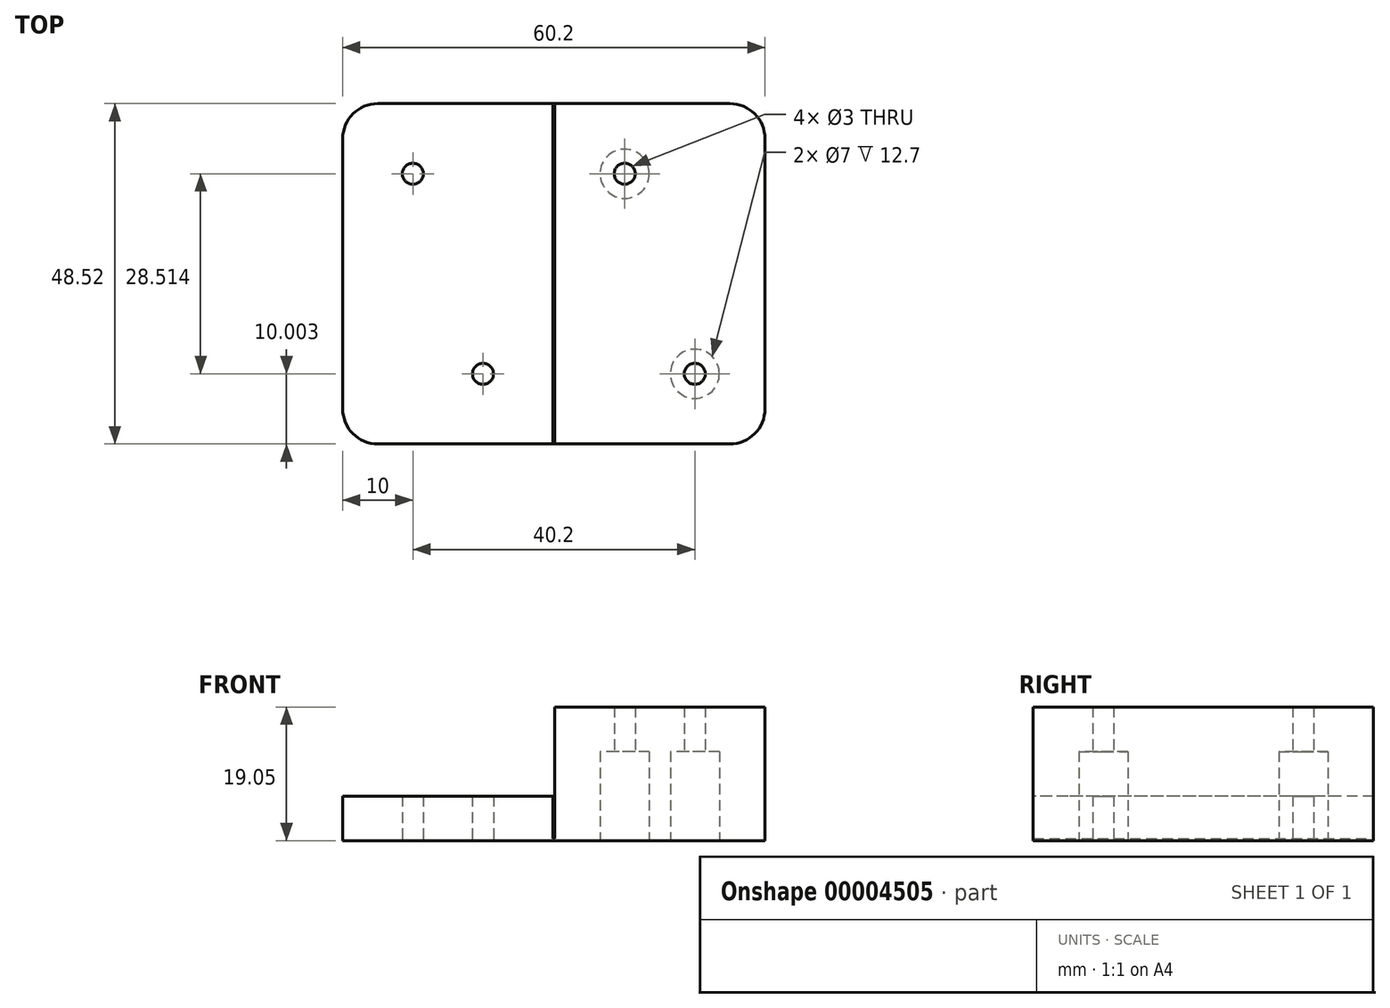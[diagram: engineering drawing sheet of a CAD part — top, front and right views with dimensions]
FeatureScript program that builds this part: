
annotation { "Feature Type Name" : "Feature", "Feature Type Description" : "" }
export const myFeature = defineFeature(function(context is Context, id is Id, definition is map)
    precondition{}
    {
        {
            var Q0;
            Q0=qCreatedBy(makeId("Top.planeOp"),FACE);
            var sketch = newSketch(context, id + "F0", { "sketchPlane" : qUnion([Q0])});
            skLineSegment(sketch, "E0.rect.bottom", {"start": v(30.1, 24.26) * mm, "end": v(-30.1, 24.26) * mm});
            skLineSegment(sketch, "E0.rect.top", {"start": v(30.1, -24.26) * mm, "end": v(-30.1, -24.26) * mm});
            skLineSegment(sketch, "E0.rect.left", {"start": v(30.1, 24.26) * mm, "end": v(30.1, -24.26) * mm});
            skLineSegment(sketch, "E0.rect.right", {"start": v(-30.1, 24.26) * mm, "end": v(-30.1, -24.26) * mm});
            skPoint(sketch, "E0.rect.middle", {"position": v(0, 0) * mm});
            skSolve(sketch);
        }
        {
            var Q0;
            Q0 = qSketchRegion(id + "F0", true);
            extrude(context, id + "F1", {"entities" : qUnion([Q0]), "depth" : .3 * mm});
        }
        {
            var Q0;
            Q0=qCreatedBy(makeId("Top.planeOp"),FACE);
            var sketch = newSketch(context, id + "F2", { "sketchPlane" : qUnion([Q0])});
            skLineSegment(sketch, "E1.bottom", {"start": v(30.1, 24.26) * mm, "end": v(0.1, 24.26) * mm});
            skLineSegment(sketch, "E1.top", {"start": v(30.1, -24.26) * mm, "end": v(0.1, -24.26) * mm});
            skLineSegment(sketch, "E1.left", {"start": v(30.1, 24.26) * mm, "end": v(30.1, -24.26) * mm});
            skLineSegment(sketch, "E1.right", {"start": v(0.1, 24.26) * mm, "end": v(0.1, -24.26) * mm});
            skSolve(sketch);
        }
        {
            var Q0;
            Q0 = qSketchRegion(id + "F2", true);
            extrude(context, id + "F3", {"entities" : qUnion([Q0]), "operationType" : NewBodyOperationType.ADD, "depth" : 19.05 * mm});
        }
        {
            var Q0;
            Q0=qCreatedBy(makeId("Top.planeOp"),FACE);
            var sketch = newSketch(context, id + "F4", { "sketchPlane" : qUnion([Q0])});
            skLineSegment(sketch, "E2.bottom", {"start": v(-30.1, 24.26) * mm, "end": v(-0.1, 24.26) * mm});
            skLineSegment(sketch, "E2.top", {"start": v(-30.1, -24.26) * mm, "end": v(-0.1, -24.26) * mm});
            skLineSegment(sketch, "E2.left", {"start": v(-30.1, 24.26) * mm, "end": v(-30.1, -24.26) * mm});
            skLineSegment(sketch, "E2.right", {"start": v(-0.1, 24.26) * mm, "end": v(-0.1, -24.26) * mm});
            skSolve(sketch);
        }
        {
            var Q0;
            Q0 = qSketchRegion(id + "F4", true);
            extrude(context, id + "F5", {"entities" : qUnion([Q0]), "operationType" : NewBodyOperationType.ADD, "depth" : 6.35 * mm});
        }
        {
            var Q0;
            Q0=qCreatedBy(makeId("Top.planeOp"),FACE);
            var sketch = newSketch(context, id + "F6", { "sketchPlane" : qUnion([Q0])});
            skCircle(sketch, "E3", {"center": v(10.1, 14.26) * mm, "radius": 1.5 * mm});
            skCircle(sketch, "E4", {"center": v(20.1, -14.26) * mm, "radius": 1.5 * mm});
            skCircle(sketch, "E5.1.0.0", {"center": v(-10.1, -14.26) * mm, "radius": 1.5 * mm});
            skCircle(sketch, "E5.1.0.1", {"center": v(-20.1, 14.26) * mm, "radius": 1.5 * mm});
            skLineSegment(sketch, "E5.direction1", {"start": v(20.1, -14.26) * mm, "end": v(-10.1, -14.26) * mm, "construction": true});
            skSolve(sketch);
        }
        {
            var Q0;
            Q0 = qSketchRegion(id + "F6", true);
            extrude(context, id + "F7", {"entities" : qUnion([Q0]), "operationType" : NewBodyOperationType.REMOVE, "endBound" : BoundingType.THROUGH_ALL, "depth" : 25 * mm});
        }
        {
            var Q0;
            Q0=qCreatedBy(makeId("Top.planeOp"),FACE);
            var sketch = newSketch(context, id + "F8", { "sketchPlane" : qUnion([Q0])});
            skCircle(sketch, "E6", {"center": v(10.1, 14.26) * mm, "radius": 3.5 * mm});
            skCircle(sketch, "E7", {"center": v(20.1, -14.26) * mm, "radius": 3.5 * mm});
            skSolve(sketch);
        }
        {
            var Q0;
            Q0 = qSketchRegion(id + "F8", true);
            extrude(context, id + "F9", {"entities" : qUnion([Q0]), "operationType" : NewBodyOperationType.REMOVE, "depth" : 12.7 * mm});
        }
        {
            var Q0;
            Q0=makeQuery(id+"F3.boolean.opBoolean","MERGE",EDGE,{"derivedFrom":[makeQuery(id+"F1.opExtrude","SWEPT_EDGE",EDGE,{"disambiguationData":[OSD([sQuery(id+"F0.wireOp",EDGE,"E0.rect.bottom"),sQuery(id+"F0.wireOp",EDGE,"E0.rect.left")])]}),makeQuery(id+"F3.opExtrude","SWEPT_EDGE",EDGE,{"disambiguationData":[OSD([sQuery(id+"F2.wireOp",EDGE,"E1.bottom"),sQuery(id+"F2.wireOp",EDGE,"E1.left")])]})]});
            var Q1;
            Q1=makeQuery(id+"F5.boolean.opBoolean","MERGE",EDGE,{"derivedFrom":[makeQuery(id+"F1.opExtrude","SWEPT_EDGE",EDGE,{"disambiguationData":[OSD([sQuery(id+"F0.wireOp",EDGE,"E0.rect.bottom"),sQuery(id+"F0.wireOp",EDGE,"E0.rect.right")])]}),makeQuery(id+"F5.opExtrude","SWEPT_EDGE",EDGE,{"disambiguationData":[OSD([sQuery(id+"F4.wireOp",EDGE,"E2.bottom"),sQuery(id+"F4.wireOp",EDGE,"E2.left")])]})]});
            var Q2;
            Q2=makeQuery(id+"F5.boolean.opBoolean","MERGE",EDGE,{"derivedFrom":[makeQuery(id+"F1.opExtrude","SWEPT_EDGE",EDGE,{"disambiguationData":[OSD([sQuery(id+"F0.wireOp",EDGE,"E0.rect.top"),sQuery(id+"F0.wireOp",EDGE,"E0.rect.right")])]}),makeQuery(id+"F5.opExtrude","SWEPT_EDGE",EDGE,{"disambiguationData":[OSD([sQuery(id+"F4.wireOp",EDGE,"E2.top"),sQuery(id+"F4.wireOp",EDGE,"E2.left")])]})]});
            var Q3;
            Q3=makeQuery(id+"F3.boolean.opBoolean","MERGE",EDGE,{"derivedFrom":[makeQuery(id+"F1.opExtrude","SWEPT_EDGE",EDGE,{"disambiguationData":[OSD([sQuery(id+"F0.wireOp",EDGE,"E0.rect.top"),sQuery(id+"F0.wireOp",EDGE,"E0.rect.left")])]}),makeQuery(id+"F3.opExtrude","SWEPT_EDGE",EDGE,{"disambiguationData":[OSD([sQuery(id+"F2.wireOp",EDGE,"E1.top"),sQuery(id+"F2.wireOp",EDGE,"E1.left")])]})]});
            fillet(context, id + "F10", {"entities" : qUnion([Q0, Q1, Q2, Q3]), "radius" : 5 * mm, "tangentPropagation" : true, "allowEdgeOverflow" : false});
        }
    });
